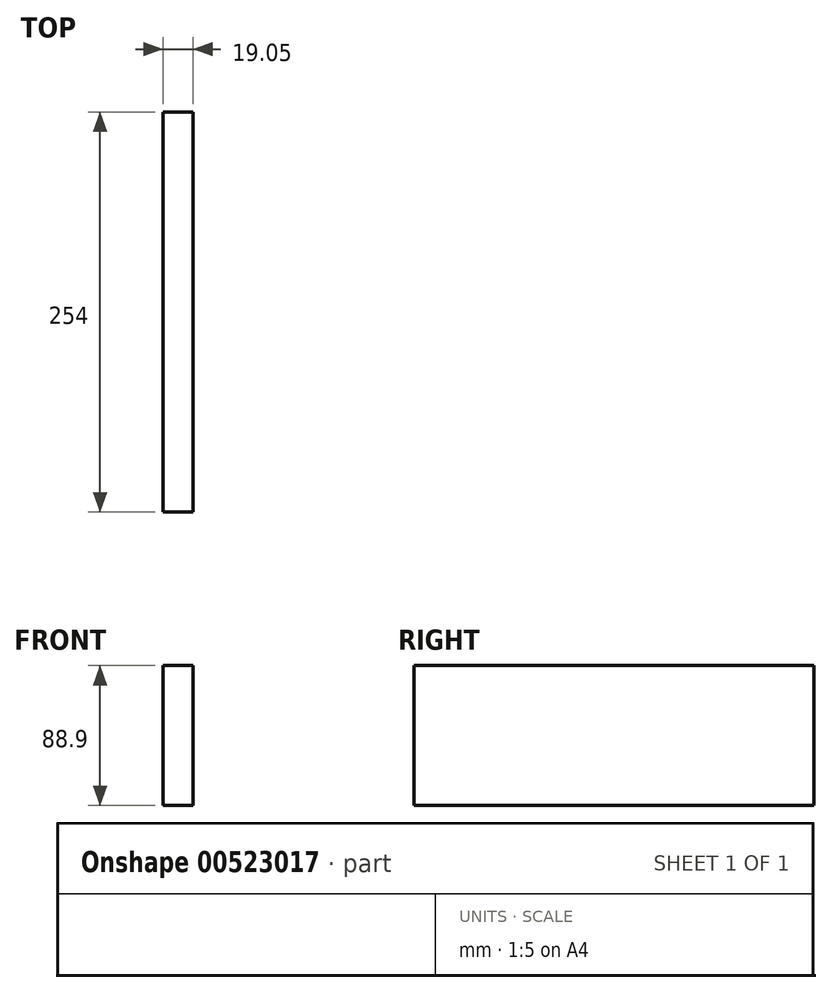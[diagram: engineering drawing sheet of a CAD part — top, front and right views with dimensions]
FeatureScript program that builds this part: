
annotation { "Feature Type Name" : "Feature", "Feature Type Description" : "" }
export const myFeature = defineFeature(function(context is Context, id is Id, definition is map)
    precondition{}
    {
        {
            var Q0;
            Q0=qCreatedBy(makeId("Front.planeOp"),FACE);
            var sketch = newSketch(context, id + "F0", { "sketchPlane" : qUnion([Q0])});
            skLineSegment(sketch, "E0.bottom", {"start": v(0, 0) * mm, "end": v(19.05, 0) * mm});
            skLineSegment(sketch, "E0.top", {"start": v(0, 88.9) * mm, "end": v(19.05, 88.9) * mm});
            skLineSegment(sketch, "E0.left", {"start": v(0, 0) * mm, "end": v(0, 88.9) * mm});
            skLineSegment(sketch, "E0.right", {"start": v(19.05, 0) * mm, "end": v(19.05, 88.9) * mm});
            skSolve(sketch);
        }
        {
            var Q0;
            Q0 = qSketchRegion(id + "F0", true);
            extrude(context, id + "F1", {"entities" : qUnion([Q0]), "endBound" : BoundingType.SYMMETRIC, "depth" : 254 * mm, "offsetDistance" : 25.4 * mm});
        }
    });
